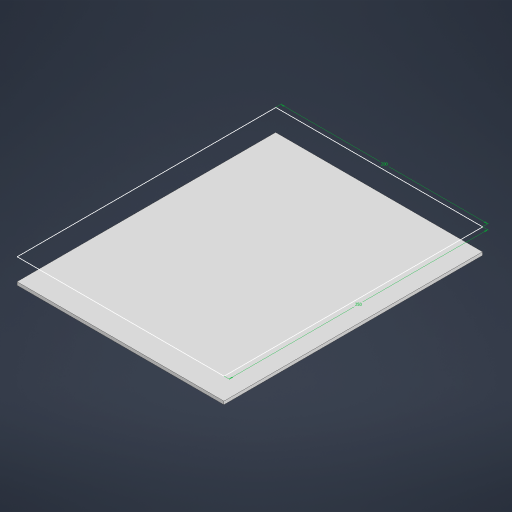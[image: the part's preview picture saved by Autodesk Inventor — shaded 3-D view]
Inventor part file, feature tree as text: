
AUTODESK INVENTOR PART (.ipt)
format: ipt  version: 2023 (Build 270158000, 158)  size: 219,648 bytes
history: native  units: mm
features: extrude x4, other x2, sketch x2, shell x1, chamfer x1
ambient origin geometry x8: Origin, YZ Plane, XZ Plane, XY Plane, X Axis, Y Axis, Z Axis, Center Point
bodies: Body1 (feature_tree)
feature tree (10):
  other  "block"
  extrude  "ext_block"  Depth=250.0mm
  shell  "Shell2"  Thickness=12.0mm
  extrude  "holes"  Depth=3.0mm
  extrude  "pwr_button_hole"  Depth=3.0mm
  chamfer  "back_cover_support"  Distance=17.0mm
  extrude  "back_cover_cut"  Depth=3.0mm
  other  "lines_base"
  sketch  "Sketch4"  dims[d0=200.0mm d1=250.0mm d2=12.0mm]
  sketch  "Sketch5"  dims[d3=12.0mm d4=25.0mm d5=17.0mm d6=17.0mm d7=25.0mm d8=75.0mm d9=80.0mm d10=65.0mm d11=60.0mm d12=6.0mm d13=84.0mm d14=90.0deg d15=25.0mm d16=125.0mm d17=70.0mm d19=14.0mm d20=10.0mm d22=10.0mm d24=5.0mm d25=10.0mm d26=65.0mm d27=95.0mm d31=200.0mm d32=250.0mm d35=24.0mm d36=0.0mm d37=3.0mm d38=24.0mm d39=0.0mm d40=19.0mm d41=13.0mm d42=4.0mm d43=12.0mm d44=24.0mm d45=0.0mm d46=4.0mm d47=2.0mm d48=45.0deg d49=0.0mm d50=0.0mm d33=0.5mm d34=0.872665mm]
